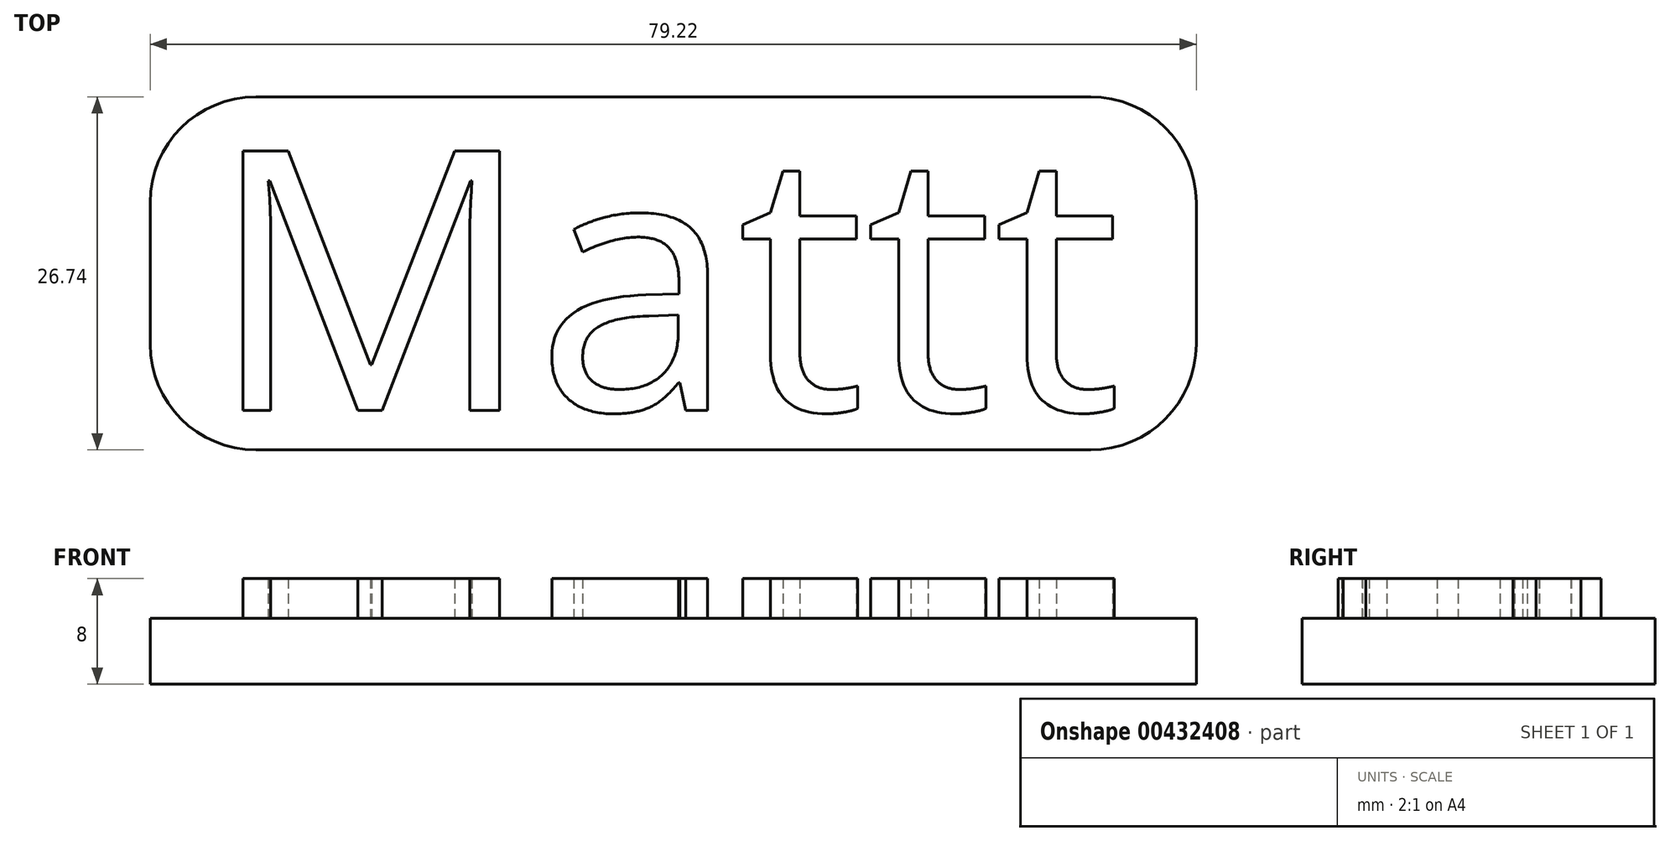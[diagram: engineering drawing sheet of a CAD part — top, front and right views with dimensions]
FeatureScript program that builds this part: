
annotation { "Feature Type Name" : "Feature", "Feature Type Description" : "" }
export const myFeature = defineFeature(function(context is Context, id is Id, definition is map)
    precondition{}
    {
        {
            var Q0;
            Q0=qCreatedBy(makeId("Top.planeOp"),FACE);
            var sketch = newSketch(context, id + "F0", { "sketchPlane" : qUnion([Q0])});
            skLineSegment(sketch, "E0.bottom", {"start": v(-39.6, 13.37) * mm, "end": v(39.6, 13.37) * mm});
            skLineSegment(sketch, "E0.top", {"start": v(-39.6, -13.37) * mm, "end": v(39.6, -13.37) * mm});
            skLineSegment(sketch, "E0.left", {"start": v(-39.6, 13.37) * mm, "end": v(-39.6, -13.37) * mm});
            skLineSegment(sketch, "E0.right", {"start": v(39.6, 13.37) * mm, "end": v(39.6, -13.37) * mm});
            skPoint(sketch, "E0.middle", {"position": v(0, 0) * mm});
            skText(sketch, "E1", { "text": "Mattt", "fontName": "OpenSans-Regular.ttf"});
            const initialGuessF0  = {"E1": [-0.03528, -0.01037, 1, 0, 0.0198]};
            skSetInitialGuess(sketch, initialGuessF0);
            skSolve(sketch);
        }
        {
            var Q0;
            Q0=makeQuery(id+"F0.imprint","IMPRINT",FACE,{"disambiguationData":[TD([[makeQuery(id+"F0.imprint","IMPRINT",EDGE,{"derivedFrom":sQuery(id+"F0.wireOp",EDGE,"E1.sketch_text.stroke-0")}),-1.0]])]});
            var Q1;
            Q1=makeQuery(id+"F0.imprint","IMPRINT",FACE,{"disambiguationData":[TD([[makeQuery(id+"F0.imprint","IMPRINT",EDGE,{"derivedFrom":sQuery(id+"F0.wireOp",EDGE,"E1.sketch_text.stroke-37")}),1.0]])]});
            var Q2;
            Q2=makeQuery(id+"F0.imprint","IMPRINT",FACE,{"disambiguationData":[TD([[makeQuery(id+"F0.imprint","IMPRINT",EDGE,{"derivedFrom":sQuery(id+"F0.wireOp",EDGE,"E1.sketch_text.stroke-45")}),-1.0]])]});
            var Q3;
            Q3=makeQuery(id+"F0.imprint","IMPRINT",FACE,{"disambiguationData":[TD([[makeQuery(id+"F0.imprint","IMPRINT",EDGE,{"derivedFrom":sQuery(id+"F0.wireOp",EDGE,"E1.sketch_text.stroke-64")}),-1.0]])]});
            var Q4;
            Q4=makeQuery(id+"F0.imprint","IMPRINT",FACE,{"disambiguationData":[TD([[makeQuery(id+"F0.imprint","IMPRINT",EDGE,{"derivedFrom":sQuery(id+"F0.wireOp",EDGE,"E1.sketch_text.stroke-83")}),-1.0]])]});
            var Q5;
            Q5=makeQuery(id+"F0.imprint","IMPRINT",FACE,{"disambiguationData":[TD([[makeQuery(id+"F0.imprint","IMPRINT",EDGE,{"derivedFrom":sQuery(id+"F0.wireOp",EDGE,"E1.sketch_text.stroke-18")}),-1.0]])]});
            var Q6;
            Q6=makeQuery(id+"F0.imprint","IMPRINT",FACE,{"disambiguationData":[TD([[makeQuery(id+"F0.imprint","IMPRINT",EDGE,{"derivedFrom":sQuery(id+"F0.wireOp",EDGE,"E0.bottom")}),-1.0]])]});
            extrude(context, id + "F1", {"entities" : qUnion([Q0, Q1, Q2, Q3, Q4, Q5, Q6]), "depth" : 5 * mm});
        }
        {
            var Q0;
            Q0=makeQuery(id+"F0.imprint","IMPRINT",FACE,{"disambiguationData":[TD([[makeQuery(id+"F0.imprint","IMPRINT",EDGE,{"derivedFrom":sQuery(id+"F0.wireOp",EDGE,"E1.sketch_text.stroke-45")}),-1.0]])]});
            var Q1;
            Q1=makeQuery(id+"F0.imprint","IMPRINT",FACE,{"disambiguationData":[TD([[makeQuery(id+"F0.imprint","IMPRINT",EDGE,{"derivedFrom":sQuery(id+"F0.wireOp",EDGE,"E1.sketch_text.stroke-64")}),-1.0]])]});
            var Q2;
            Q2=makeQuery(id+"F0.imprint","IMPRINT",FACE,{"disambiguationData":[TD([[makeQuery(id+"F0.imprint","IMPRINT",EDGE,{"derivedFrom":sQuery(id+"F0.wireOp",EDGE,"E1.sketch_text.stroke-83")}),-1.0]])]});
            var Q3;
            Q3=makeQuery(id+"F0.imprint","IMPRINT",FACE,{"disambiguationData":[TD([[makeQuery(id+"F0.imprint","IMPRINT",EDGE,{"derivedFrom":sQuery(id+"F0.wireOp",EDGE,"E1.sketch_text.stroke-18")}),-1.0]])]});
            var Q4;
            Q4=makeQuery(id+"F0.imprint","IMPRINT",FACE,{"disambiguationData":[TD([[makeQuery(id+"F0.imprint","IMPRINT",EDGE,{"derivedFrom":sQuery(id+"F0.wireOp",EDGE,"E1.sketch_text.stroke-0")}),-1.0]])]});
            extrude(context, id + "F2", {"entities" : qUnion([Q0, Q1, Q2, Q3, Q4]), "operationType" : NewBodyOperationType.ADD, "depth" : 8 * mm});
        }
        {
            var Q0;
            Q0=makeQuery(id+"F1.opExtrude","SWEPT_EDGE",EDGE,{"disambiguationData":[OSD([sQuery(id+"F0.wireOp",EDGE,"E0.top"),sQuery(id+"F0.wireOp",EDGE,"E0.left")])]});
            var Q1;
            Q1=makeQuery(id+"F1.opExtrude","SWEPT_EDGE",EDGE,{"disambiguationData":[OSD([sQuery(id+"F0.wireOp",EDGE,"E0.bottom"),sQuery(id+"F0.wireOp",EDGE,"E0.left")])]});
            var Q2;
            Q2=makeQuery(id+"F1.opExtrude","SWEPT_EDGE",EDGE,{"disambiguationData":[OSD([sQuery(id+"F0.wireOp",EDGE,"E0.top"),sQuery(id+"F0.wireOp",EDGE,"E0.right")])]});
            var Q3;
            Q3=makeQuery(id+"F1.opExtrude","SWEPT_EDGE",EDGE,{"disambiguationData":[OSD([sQuery(id+"F0.wireOp",EDGE,"E0.bottom"),sQuery(id+"F0.wireOp",EDGE,"E0.right")])]});
            fillet(context, id + "F3", {"entities" : qUnion([Q0, Q1, Q2, Q3]), "radius" : 8 * mm, "tangentPropagation" : true, "allowEdgeOverflow" : false});
        }
    });
